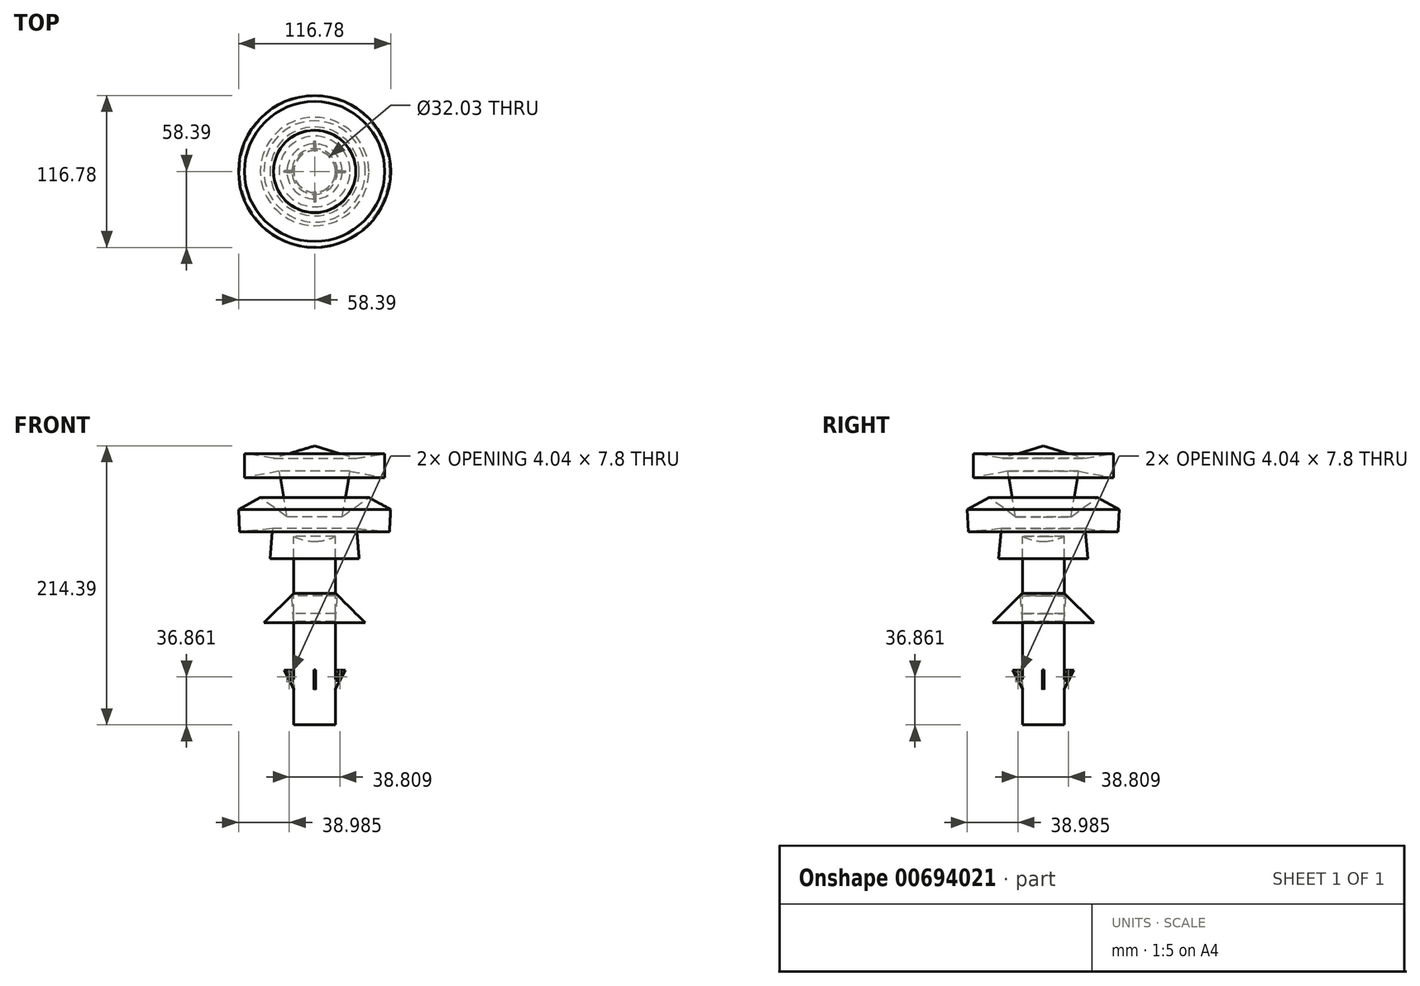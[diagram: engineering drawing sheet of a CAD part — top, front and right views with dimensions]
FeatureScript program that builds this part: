
annotation { "Feature Type Name" : "Feature", "Feature Type Description" : "" }
export const myFeature = defineFeature(function(context is Context, id is Id, definition is map)
    precondition{}
    {
        {
            var Q0;
            Q0=qCreatedBy(makeId("Front.planeOp"),FACE);
            var sketch = newSketch(context, id + "F0", { "sketchPlane" : qUnion([Q0])});
            skLineSegment(sketch, "E0.bottom", {"start": v(0, 0) * mm, "end": v(16.01, 0) * mm});
            skLineSegment(sketch, "E0.top", {"start": v(0, 176.16) * mm, "end": v(16.01, 176.16) * mm});
            skLineSegment(sketch, "E0.left", {"start": v(0, 0) * mm, "end": v(0, 176.16) * mm});
            skLineSegment(sketch, "E0.right", {"start": v(16.01, 0) * mm, "end": v(16.01, 176.16) * mm});
            skArc(sketch, "E1", {"start": v(0, 141.01) * mm, "mid": v(35.15, 176.16) * mm, "end": v(0, 211.3) * mm});
            skSolve(sketch);
        }
        {
            var Q0;
            {var subQ0=sQuery(id+"F0.wireOp",EDGE,"E0.bottom");Q0=makeQuery(id+"F0.imprint","IMPRINT",FACE,{"disambiguationData":[TD([[makeQuery(id+"F0.imprint","IMPRINT",EDGE,{"derivedFrom":subQ0}),1.0]])]});}
            var sketch = newSketch(context, id + "F1", { "sketchPlane" : qUnion([Q0])});
            skLineSegment(sketch, "E2", {"start": v(16.18, 101.06) * mm, "end": v(38.92, 78.34) * mm});
            skLineSegment(sketch, "E3", {"start": v(38.92, 78.34) * mm, "end": v(15.94, 78.34) * mm});
            skLineSegment(sketch, "E4", {"start": v(15.94, 78.34) * mm, "end": v(15.94, 78.34) * mm});
            skLineSegment(sketch, "E5", {"start": v(17.52, 99.13) * mm, "end": v(16.18, 101.06) * mm});
            skLineSegment(sketch, "E6", {"start": v(17.52, 99.13) * mm, "end": v(15.94, 78.34) * mm});
            skLineSegment(sketch, "E7", {"start": v(16.18, 101.06) * mm, "end": v(15.94, 78.34) * mm});
            skSolve(sketch);
        }
        {
            var Q0;
            Q0 = qSketchRegion(id + "F0", true);
            var sketch = newSketch(context, id + "F2", { "sketchPlane" : qUnion([Q0])});
            skLineSegment(sketch, "E8", {"start": v(15.74, 27.1) * mm, "end": v(23.52, 41.97) * mm});
            skLineSegment(sketch, "E9", {"start": v(23.52, 41.97) * mm, "end": v(23.52, 41.97) * mm});
            skLineSegment(sketch, "E10", {"start": v(16.27, 42.42) * mm, "end": v(23.52, 41.97) * mm});
            skLineSegment(sketch, "E11", {"start": v(16.27, 42.42) * mm, "end": v(15.74, 27.1) * mm});
            skLineSegment(sketch, "E12", {"start": v(17.63, 39.9) * mm, "end": v(17.39, 32.96) * mm});
            skLineSegment(sketch, "E13", {"start": v(17.39, 32.96) * mm, "end": v(21.42, 40.76) * mm});
            skLineSegment(sketch, "E14", {"start": v(21.42, 40.76) * mm, "end": v(17.63, 39.9) * mm});
            skSolve(sketch);
        }
        {
            var Q0;
            Q0 = qSketchRegion(id + "F2", true);
            extrude(context, id + "F3", {"entities" : qUnion([Q0]), "endBound" : BoundingType.SYMMETRIC, "oppositeDirection" : true, "depth" : 1.3 * mm, "offsetDistance" : 25.4 * mm});
        }
        {
            var Q0;
            Q0=makeQuery(id+"F3.opExtrude","SWEPT_BODY",BODY,{"disambiguationData":[OSD([sQuery(id+"F2.wireOp",EDGE,"E8"),sQuery(id+"F2.wireOp",EDGE,"E10"),sQuery(id+"F2.wireOp",EDGE,"E11"),sQuery(id+"F2.wireOp",EDGE,"E12"),sQuery(id+"F2.wireOp",EDGE,"E13"),sQuery(id+"F2.wireOp",EDGE,"E14")])]});
            var Q1;
            Q1=sQuery(id+"F0.wireOp",EDGE,"E0.left");
            circularPattern(context, id + "F4", {"entities" : qUnion([Q0]), "axis" : qUnion([Q1]), "angle" : 360 * degree, "instanceCount" : 4, "equalSpace" : true});
        }
        {
            var Q0;
            Q0 = qSketchRegion(id + "F0", true);
            var sketch = newSketch(context, id + "F5", { "sketchPlane" : qUnion([Q0])});
            skLineSegment(sketch, "E15", {"start": v(0, 214.4) * mm, "end": v(0, 138.77) * mm});
            skLineSegment(sketch, "E16", {"start": v(0, 138.77) * mm, "end": v(0, 127.7) * mm});
            skLineSegment(sketch, "E17", {"start": v(0, 127.7) * mm, "end": v(-34.2, 127.7) * mm});
            skLineSegment(sketch, "E18", {"start": v(-34.2, 127.7) * mm, "end": v(-32.26, 150.83) * mm});
            skLineSegment(sketch, "E19", {"start": v(-32.26, 150.83) * mm, "end": v(-57.52, 148.17) * mm});
            skLineSegment(sketch, "E20", {"start": v(-57.52, 148.17) * mm, "end": v(-58.4, 165.58) * mm});
            skLineSegment(sketch, "E21", {"start": v(-58.4, 165.58) * mm, "end": v(-41.65, 174.63) * mm});
            skLineSegment(sketch, "E22", {"start": v(-41.65, 174.63) * mm, "end": v(-21.17, 159.9) * mm});
            skLineSegment(sketch, "E23", {"start": v(-21.17, 159.9) * mm, "end": v(-27.2, 194.92) * mm});
            skLineSegment(sketch, "E24", {"start": v(-27.2, 194.92) * mm, "end": v(-53.83, 189.89) * mm});
            skLineSegment(sketch, "E25", {"start": v(-53.83, 189.89) * mm, "end": v(-53.82, 208.45) * mm});
            skLineSegment(sketch, "E26", {"start": v(-53.82, 208.45) * mm, "end": v(-31.6, 204.79) * mm});
            skLineSegment(sketch, "E27", {"start": v(-31.6, 204.79) * mm, "end": v(0, 214.4) * mm});
            skSolve(sketch);
        }
        {
            var Q0;
            {var subQ5=sQuery(id+"F5.wireOp",EDGE,"E16");Q0=makeQuery(id+"F5.imprint","IMPRINT",FACE,{"disambiguationData":[TD([[makeQuery(id+"F5.imprint","IMPRINT",EDGE,{"derivedFrom":subQ5}),1.0]])]});}
            var Q1;
            {var subQ1=sQuery(id+"F0.wireOp",EDGE,"E0.bottom");var subQ4=makeQuery(id+"F0.imprint","IMPRINT",EDGE,{"derivedFrom":subQ1});Q1=makeQuery(id+"F1.imprint","IMPRINT",FACE,{"disambiguationData":[TD([[makeQuery(id+"F1.imprint","IMPRINT",EDGE,{"derivedFrom":subQ4}),1.0]])]});}
            var Q2;
            {var subQ6=sQuery(id+"F1.wireOp",EDGE,"E2");Q2=makeQuery(id+"F1.imprint","IMPRINT",FACE,{"disambiguationData":[TD([[makeQuery(id+"F1.imprint","IMPRINT",EDGE,{"derivedFrom":subQ6}),-1.0]])]});}
            var Q3;
            Q3=sQuery(id+"F5.wireOp",EDGE,"E15");
            revolve(context, id + "F6", {"entities" : qUnion([Q0, Q1, Q2]), "axis" : qUnion([Q3]), "revolveType" : RevolveType.FULL});
        }
    });
